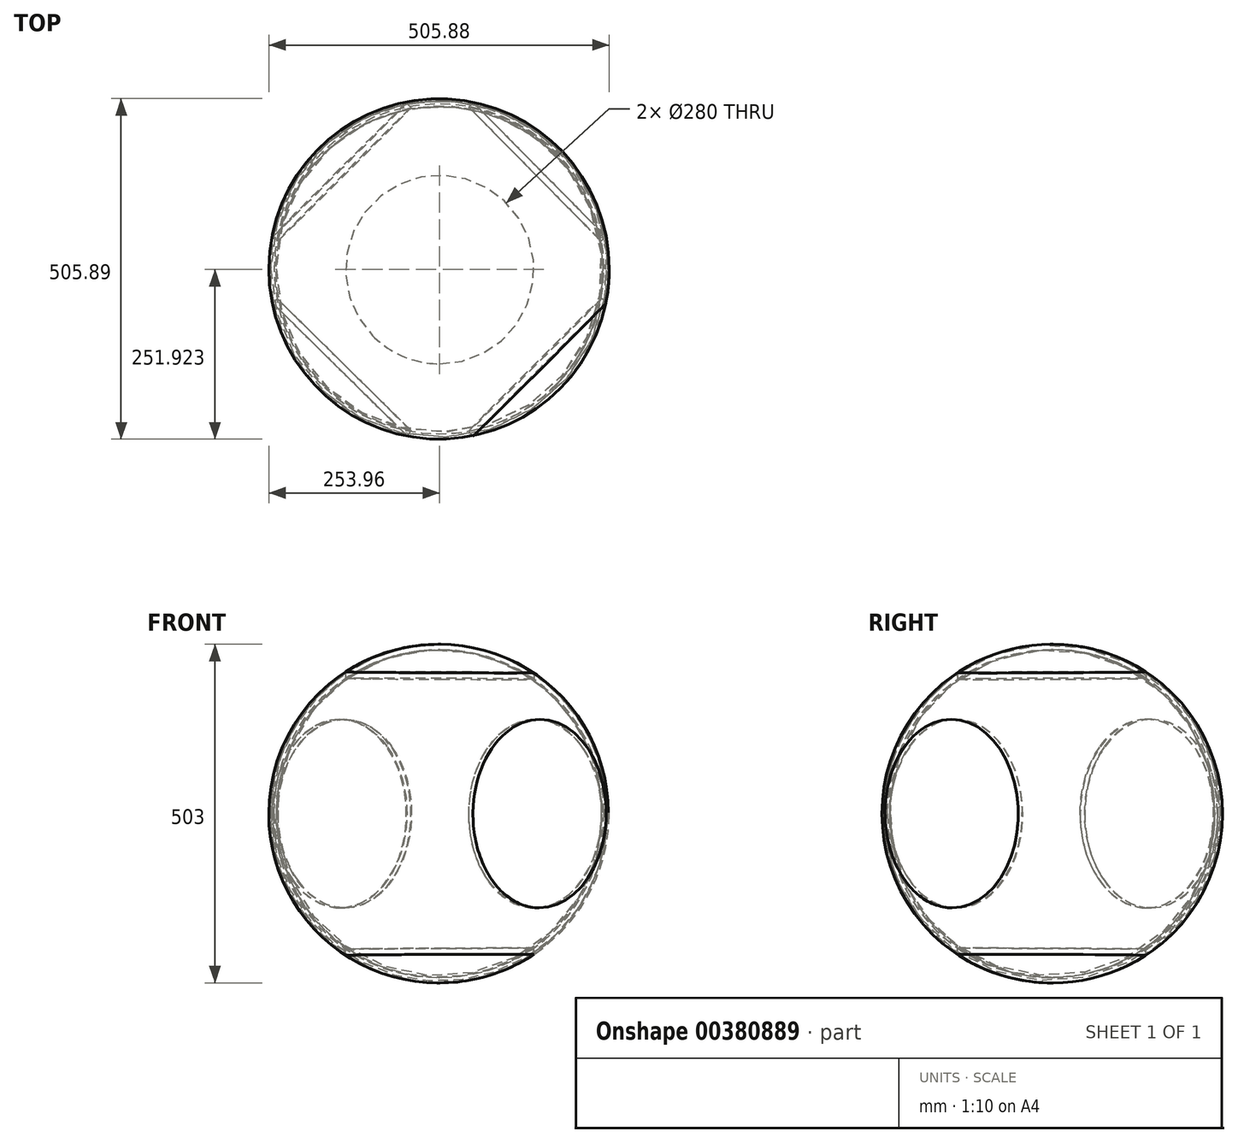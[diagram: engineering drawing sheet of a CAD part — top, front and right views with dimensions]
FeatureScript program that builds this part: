
annotation { "Feature Type Name" : "Feature", "Feature Type Description" : "" }
export const myFeature = defineFeature(function(context is Context, id is Id, definition is map)
    precondition{}
    {
        {
            var Q0;
            Q0=qCreatedBy(makeId("Right.planeOp"),FACE);
            var sketch = newSketch(context, id + "F0", { "sketchPlane" : qUnion([Q0])});
            skCircle(sketch, "E0", {"center": v(0, 0) * mm, "radius": 243.58 * mm});
            skLineSegment(sketch, "E1", {"start": v(1.44, 243.58) * mm, "end": v(1.44, -243.58) * mm});
            skCircle(sketch, "E2", {"center": v(0, 0) * mm, "radius": 251.5 * mm});
            skLineSegment(sketch, "E3", {"start": v(1.44, 243.58) * mm, "end": v(1.44, -357.35) * mm});
            skLineSegment(sketch, "E4", {"start": v(1.44, -357.35) * mm, "end": v(1.44, 517.62) * mm});
            skSolve(sketch);
        }
        {
            var Q0;
            {var subQ0=sQuery(id+"F0.wireOp",EDGE,"E4");var subQ1=sQuery(id+"F0.wireOp",EDGE,"E0");var subQ2=makeQuery(id+"F0.imprint","INTERSECT",VERTEX,{"disambiguationData":[OD(0.0)],"derivedFrom":[subQ1,subQ0]});Q0=makeQuery(id+"F0.imprint","IMPRINT",FACE,{"disambiguationData":[TD([[makeQuery(id+"F0.imprint","IMPRINT",EDGE,{"disambiguationData":[TD([[subQ2,-1.0]])],"derivedFrom":subQ1}),-1.0]])]});}
            var Q1;
            Q1=sQuery(id+"F0.wireOp",EDGE,"E4");
            revolve(context, id + "F1", {"entities" : qUnion([Q0]), "axis" : qUnion([Q1]), "revolveType" : RevolveType.FULL});
        }
        {
            var Q0;
            Q0=qCreatedBy(makeId("Top.planeOp"),FACE);
            var sketch = newSketch(context, id + "F2", { "sketchPlane" : qUnion([Q0])});
            skCircle(sketch, "E5", {"center": v(0, 0) * mm, "radius": 140 * mm});
            skLineSegment(sketch, "E6", {"start": v(0, -77.93) * mm, "end": v(0, 75.7) * mm});
            skLineSegment(sketch, "E7", {"start": v(-72.82, 0) * mm, "end": v(75.83, 0) * mm});
            skSolve(sketch);
        }
        {
            var Q0;
            Q0 = qSketchRegion(id + "F2", true);
            var Q1;
            Q1=sQuery(id+"F2.wireOp",EDGE,"E5");
            extrude(context, id + "F3", {"entities" : qUnion([Q0]), "operationType" : NewBodyOperationType.INTERSECT, "surfaceEntities" : qUnion([Q1]), "endBound" : BoundingType.THROUGH_ALL, "oppositeDirection" : true, "depth" : 250 * mm});
        }
        {
            var Q0;
            Q0=makeQuery(id+"F1.opRevolve","SWEPT_BODY",BODY,{"disambiguationData":[OSD([sQuery(id+"F0.wireOp",EDGE,"E0"),sQuery(id+"F0.wireOp",EDGE,"E2"),sQuery(id+"F0.wireOp",EDGE,"E4")])]});
            var Q1;
            Q1=qCreatedBy(makeId("Top.planeOp"),FACE);
            mirror(context, id + "F4", {"entities" : qUnion([Q0]), "mirrorPlane" : qUnion([Q1])});
        }
        {
            var Q0;
            Q0=makeQuery(id+"F4.opPattern","COPY",BODY,{"derivedFrom":makeQuery(id+"F1.opRevolve","SWEPT_BODY",BODY,{"disambiguationData":[OSD([sQuery(id+"F0.wireOp",EDGE,"E0"),sQuery(id+"F0.wireOp",EDGE,"E2"),sQuery(id+"F0.wireOp",EDGE,"E4")])]}),"instanceName":"1"});
            var Q1;
            Q1=makeQuery(id+"F1.opRevolve","SWEPT_BODY",BODY,{"disambiguationData":[OSD([sQuery(id+"F0.wireOp",EDGE,"E0"),sQuery(id+"F0.wireOp",EDGE,"E2"),sQuery(id+"F0.wireOp",EDGE,"E4")])]});
            var Q2;
            Q2=qCreatedBy(makeId("Top.planeOp"),FACE);
            mirror(context, id + "F5", {"entities" : qUnion([Q0, Q1]), "mirrorPlane" : qUnion([Q2])});
        }
        {
            var Q0;
            Q0=makeQuery(id+"F5.opPattern","COPY",BODY,{"derivedFrom":makeQuery(id+"F1.opRevolve","SWEPT_BODY",BODY,{"disambiguationData":[OSD([sQuery(id+"F0.wireOp",EDGE,"E0"),sQuery(id+"F0.wireOp",EDGE,"E2"),sQuery(id+"F0.wireOp",EDGE,"E4")])]}),"instanceName":"1"});
            var Q1;
            Q1=makeQuery(id+"F5.opPattern","COPY",BODY,{"derivedFrom":makeQuery(id+"F4.opPattern","COPY",BODY,{"derivedFrom":makeQuery(id+"F1.opRevolve","SWEPT_BODY",BODY,{"disambiguationData":[OSD([sQuery(id+"F0.wireOp",EDGE,"E0"),sQuery(id+"F0.wireOp",EDGE,"E2"),sQuery(id+"F0.wireOp",EDGE,"E4")])]}),"instanceName":"1"}),"instanceName":"1"});
            var Q2;
            Q2=qCreatedBy(makeId("Origin.pointOp"),VERTEX);
            var Q3;
            Q3=sQuery(id+"F2.wireOp",EDGE,"E6");
            transform(context, id + "F6", {"entities" : qUnion([Q0, Q1]), "transformType" : TransformType.ROTATION, "transformAxis" : qUnion([Q3]), "angle" : 90 * degree, "makeCopy" : true});
        }
        {
            var Q0;
            Q0=makeQuery(id+"F4.opPattern","COPY",BODY,{"derivedFrom":makeQuery(id+"F1.opRevolve","SWEPT_BODY",BODY,{"disambiguationData":[OSD([sQuery(id+"F0.wireOp",EDGE,"E0"),sQuery(id+"F0.wireOp",EDGE,"E2"),sQuery(id+"F0.wireOp",EDGE,"E4")])]}),"instanceName":"1"});
            var Q1;
            Q1=makeQuery(id+"F5.opPattern","COPY",BODY,{"derivedFrom":makeQuery(id+"F4.opPattern","COPY",BODY,{"derivedFrom":makeQuery(id+"F1.opRevolve","SWEPT_BODY",BODY,{"disambiguationData":[OSD([sQuery(id+"F0.wireOp",EDGE,"E0"),sQuery(id+"F0.wireOp",EDGE,"E2"),sQuery(id+"F0.wireOp",EDGE,"E4")])]}),"instanceName":"1"}),"instanceName":"1"});
            var Q2;
            Q2=sQuery(id+"F2.wireOp",EDGE,"E7");
            transform(context, id + "F7", {"entities" : qUnion([Q0, Q1]), "transformType" : TransformType.ROTATION, "transformAxis" : qUnion([Q2]), "angle" : 90 * degree, "makeCopy" : false});
        }
        {
            var Q0;
            {var subQ0=sQuery(id+"F0.wireOp",EDGE,"E4");var subQ1=sQuery(id+"F0.wireOp",EDGE,"E0");var subQ2=makeQuery(id+"F0.imprint","INTERSECT",VERTEX,{"disambiguationData":[OD(0.0)],"derivedFrom":[subQ1,subQ0]});Q0=makeQuery(id+"F0.imprint","IMPRINT",FACE,{"disambiguationData":[TD([[makeQuery(id+"F0.imprint","IMPRINT",EDGE,{"disambiguationData":[TD([[subQ2,-1.0]])],"derivedFrom":subQ1}),-1.0]])]});}
            var Q1;
            Q1=sQuery(id+"F0.wireOp",EDGE,"E3");
            revolve(context, id + "F8", {"entities" : qUnion([Q0]), "axis" : qUnion([Q1]), "revolveType" : RevolveType.FULL});
        }
        {
            var Q0;
            Q0=makeQuery(id+"F6.opPattern","COPY",BODY,{"derivedFrom":makeQuery(id+"F5.opPattern","COPY",BODY,{"derivedFrom":makeQuery(id+"F1.opRevolve","SWEPT_BODY",BODY,{"disambiguationData":[OSD([sQuery(id+"F0.wireOp",EDGE,"E0"),sQuery(id+"F0.wireOp",EDGE,"E2"),sQuery(id+"F0.wireOp",EDGE,"E4")])]}),"instanceName":"1"}),"instanceName":"1"});
            var Q1;
            Q1=makeQuery(id+"F6.opPattern","COPY",BODY,{"derivedFrom":makeQuery(id+"F5.opPattern","COPY",BODY,{"derivedFrom":makeQuery(id+"F4.opPattern","COPY",BODY,{"derivedFrom":makeQuery(id+"F1.opRevolve","SWEPT_BODY",BODY,{"disambiguationData":[OSD([sQuery(id+"F0.wireOp",EDGE,"E0"),sQuery(id+"F0.wireOp",EDGE,"E2"),sQuery(id+"F0.wireOp",EDGE,"E4")])]}),"instanceName":"1"}),"instanceName":"1"}),"instanceName":"1"});
            var Q2;
            Q2=makeQuery(id+"F5.opPattern","COPY",BODY,{"derivedFrom":makeQuery(id+"F4.opPattern","COPY",BODY,{"derivedFrom":makeQuery(id+"F1.opRevolve","SWEPT_BODY",BODY,{"disambiguationData":[OSD([sQuery(id+"F0.wireOp",EDGE,"E0"),sQuery(id+"F0.wireOp",EDGE,"E2"),sQuery(id+"F0.wireOp",EDGE,"E4")])]}),"instanceName":"1"}),"instanceName":"1"});
            var Q3;
            Q3=makeQuery(id+"F5.opPattern","COPY",BODY,{"derivedFrom":makeQuery(id+"F1.opRevolve","SWEPT_BODY",BODY,{"disambiguationData":[OSD([sQuery(id+"F0.wireOp",EDGE,"E0"),sQuery(id+"F0.wireOp",EDGE,"E2"),sQuery(id+"F0.wireOp",EDGE,"E4")])]}),"instanceName":"1"});
            var Q4;
            Q4=makeQuery(id+"F4.opPattern","COPY",BODY,{"derivedFrom":makeQuery(id+"F1.opRevolve","SWEPT_BODY",BODY,{"disambiguationData":[OSD([sQuery(id+"F0.wireOp",EDGE,"E0"),sQuery(id+"F0.wireOp",EDGE,"E2"),sQuery(id+"F0.wireOp",EDGE,"E4")])]}),"instanceName":"1"});
            var Q5;
            Q5=makeQuery(id+"F1.opRevolve","SWEPT_BODY",BODY,{"disambiguationData":[OSD([sQuery(id+"F0.wireOp",EDGE,"E0"),sQuery(id+"F0.wireOp",EDGE,"E2"),sQuery(id+"F0.wireOp",EDGE,"E4")])]});
            var Q6;
            Q6=sQuery(id+"F0.wireOp",EDGE,"E4");
            transform(context, id + "F9", {"entities" : qUnion([Q0, Q1, Q2, Q3, Q4, Q5]), "transformType" : TransformType.ROTATION, "transformAxis" : qUnion([Q6]), "angle" : 45 * degree, "makeCopy" : false});
        }
    });
